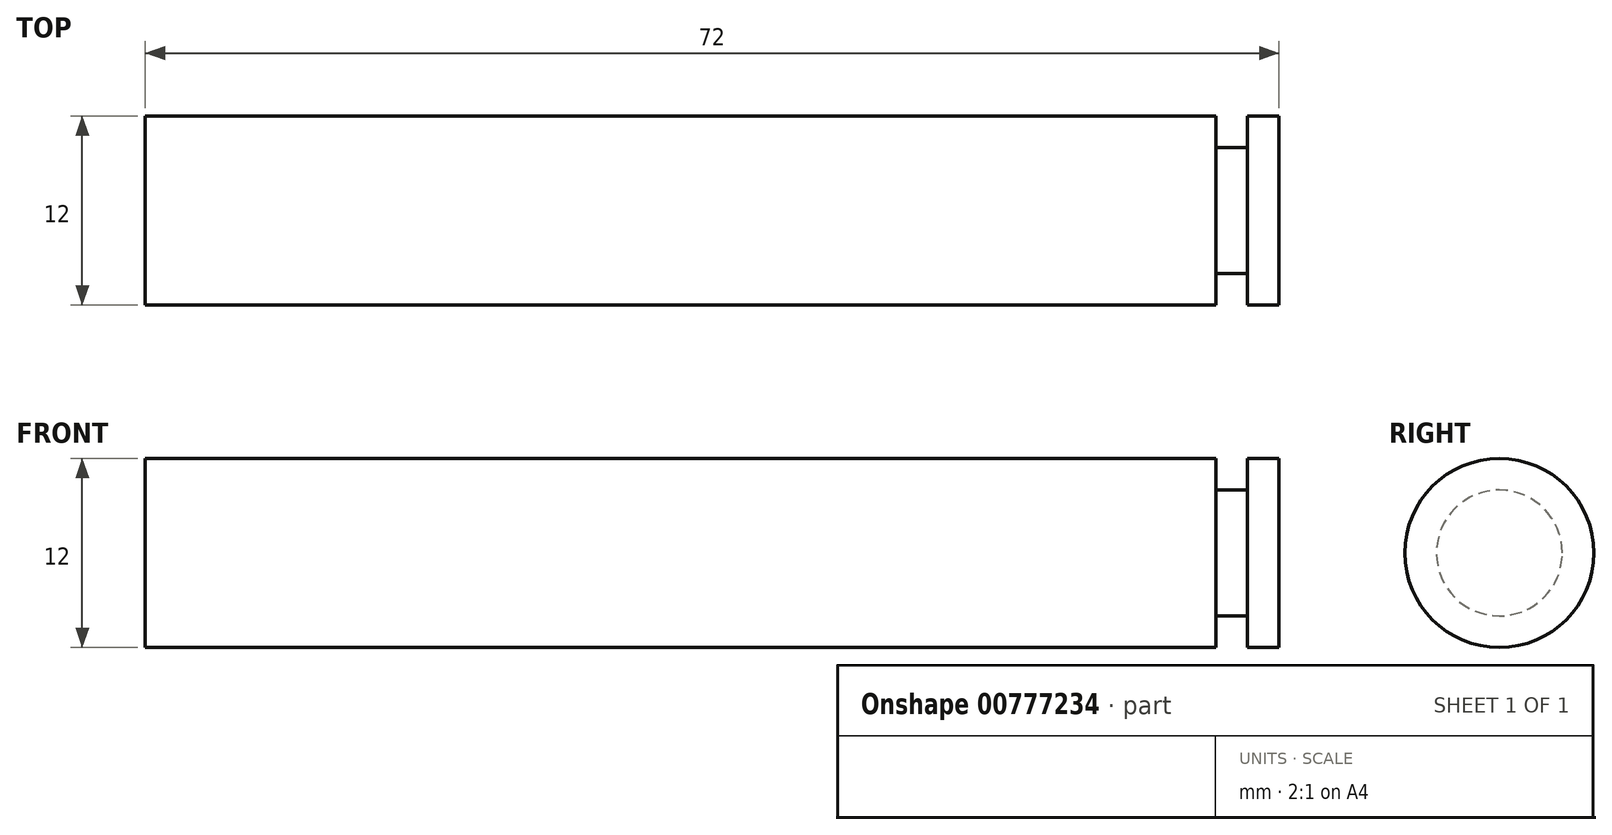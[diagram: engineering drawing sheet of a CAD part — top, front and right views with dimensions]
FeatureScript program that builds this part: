
annotation { "Feature Type Name" : "Feature", "Feature Type Description" : "" }
export const myFeature = defineFeature(function(context is Context, id is Id, definition is map)
    precondition{}
    {
        {
            var Q0;
            Q0=qCreatedBy(makeId("Front.planeOp"),FACE);
            var sketch = newSketch(context, id + "F0", { "sketchPlane" : qUnion([Q0])});
            skLineSegment(sketch, "E0.bottom", {"start": v(-28.33, 15.16) * mm, "end": v(39.67, 15.16) * mm});
            skLineSegment(sketch, "E0.top", {"start": v(-28.33, 9.16) * mm, "end": v(43.67, 9.16) * mm});
            skLineSegment(sketch, "E0.left", {"start": v(-28.33, 15.16) * mm, "end": v(-28.33, 9.16) * mm});
            skLineSegment(sketch, "E0.right", {"start": v(43.67, 15.16) * mm, "end": v(43.67, 9.16) * mm});
            skLineSegment(sketch, "E1.top", {"start": v(41.67, 13.16) * mm, "end": v(39.67, 13.16) * mm});
            skLineSegment(sketch, "E1.left", {"start": v(41.67, 15.16) * mm, "end": v(41.67, 13.16) * mm});
            skLineSegment(sketch, "E1.right", {"start": v(39.67, 15.16) * mm, "end": v(39.67, 13.16) * mm});
            skLineSegment(sketch, "E2.trimOffspring", {"start": v(41.67, 15.16) * mm, "end": v(43.67, 15.16) * mm});
            skSolve(sketch);
        }
        {
            var Q0;
            Q0=makeQuery(id+"F0.imprint","IMPRINT",FACE,{"disambiguationData":[TD([[makeQuery(id+"F0.imprint","IMPRINT",EDGE,{"derivedFrom":sQuery(id+"F0.wireOp",EDGE,"E0.bottom")}),-1.0]])]});
            var Q1;
            Q1=sQuery(id+"F0.wireOp",EDGE,"E0.top");
            revolve(context, id + "F1", {"surfaceOperationType" : NewSurfaceOperationType.NEW, "entities" : qUnion([Q0]), "axis" : qUnion([Q1]), "revolveType" : RevolveType.FULL});
        }
    });
